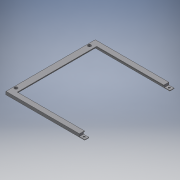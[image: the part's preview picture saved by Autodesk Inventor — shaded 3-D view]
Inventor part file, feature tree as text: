
AUTODESK INVENTOR PART (.ipt)
format: ipt  version: 2016 SP2 (Build 200236200, 236)  size: 133,120 bytes
history: native  units: mm
features: sketch x5, other x3
ambient origin geometry x8: Origin, YZ Plane, XZ Plane, XY Plane, X Axis, Y Axis, Z Axis, Center Point
bodies: Volumenkörper1 (feature_tree)
feature tree (8):
  other  "Case-Side.ipt"
  other  "Volumenkörper1::Case-Side.ipt"
  other  "Bezeichnung1"
  sketch  "Skizze1"  dims[d0=10.0mm]
  sketch  "Skizze2"
  sketch  "Skizze3"
  sketch  "Skizze4"
  sketch  "Skizze5"
